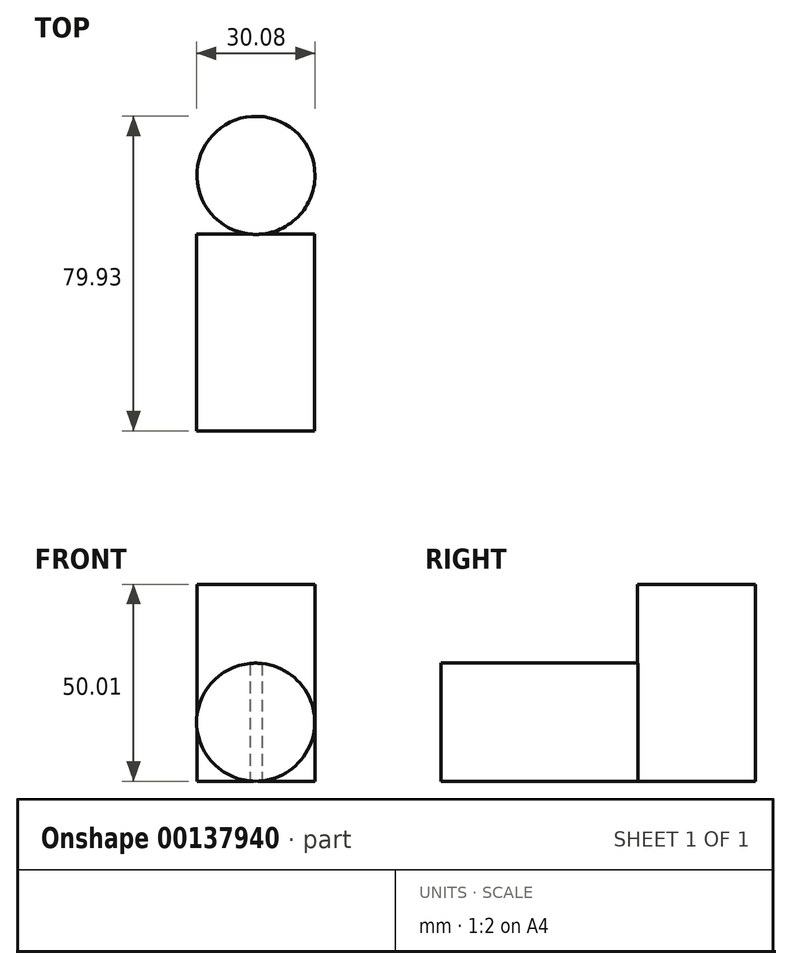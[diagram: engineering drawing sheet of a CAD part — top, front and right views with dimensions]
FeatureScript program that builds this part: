
annotation { "Feature Type Name" : "Feature", "Feature Type Description" : "" }
export const myFeature = defineFeature(function(context is Context, id is Id, definition is map)
    precondition{}
    {
        {
            var Q0;
            Q0=qCreatedBy(makeId("Front.planeOp"),FACE);
            var sketch = newSketch(context, id + "F0", { "sketchPlane" : qUnion([Q0])});
            skCircle(sketch, "E0", {"center": v(-14.98, 14.99) * mm, "radius": 15 * mm});
            skPoint(sketch, "E0.first.point", {"position": v(0, 15.77) * mm});
            skPoint(sketch, "E0.second.point", {"position": v(-29.97, 15.38) * mm});
            skPoint(sketch, "E0.third.point", {"position": v(-15.57, 0) * mm});
            skSolve(sketch);
        }
        {
            var Q0;
            Q0=makeQuery(id+"F0.imprint","IMPRINT",FACE,{"disambiguationData":[TD([[makeQuery(id+"F0.imprint","IMPRINT",EDGE,{"derivedFrom":sQuery(id+"F0.wireOp",EDGE,"E0")}),1.0]])]});
            extrude(context, id + "F1", {"entities" : qUnion([Q0]), "depth" : 50 * mm});
        }
        {
            var Q0;
            Q0=qCreatedBy(makeId("Top.planeOp"),FACE);
            var sketch = newSketch(context, id + "F2", { "sketchPlane" : qUnion([Q0])});
            skCircle(sketch, "E1", {"center": v(-14.9, 14.93) * mm, "radius": 15 * mm});
            skPoint(sketch, "E1.first.point", {"position": v(0, 13.2) * mm});
            skPoint(sketch, "E1.second.point", {"position": v(-29.68, 17.5) * mm});
            skPoint(sketch, "E1.third.point", {"position": v(-16.37, 0) * mm});
            skSolve(sketch);
        }
        {
            var Q0;
            Q0=makeQuery(id+"F2.imprint","IMPRINT",FACE,{"disambiguationData":[TD([[makeQuery(id+"F2.imprint","IMPRINT",EDGE,{"derivedFrom":sQuery(id+"F2.wireOp",EDGE,"E1")}),1.0]])]});
            extrude(context, id + "F3", {"entities" : qUnion([Q0]), "operationType" : NewBodyOperationType.ADD, "depth" : 50 * mm});
        }
    });
